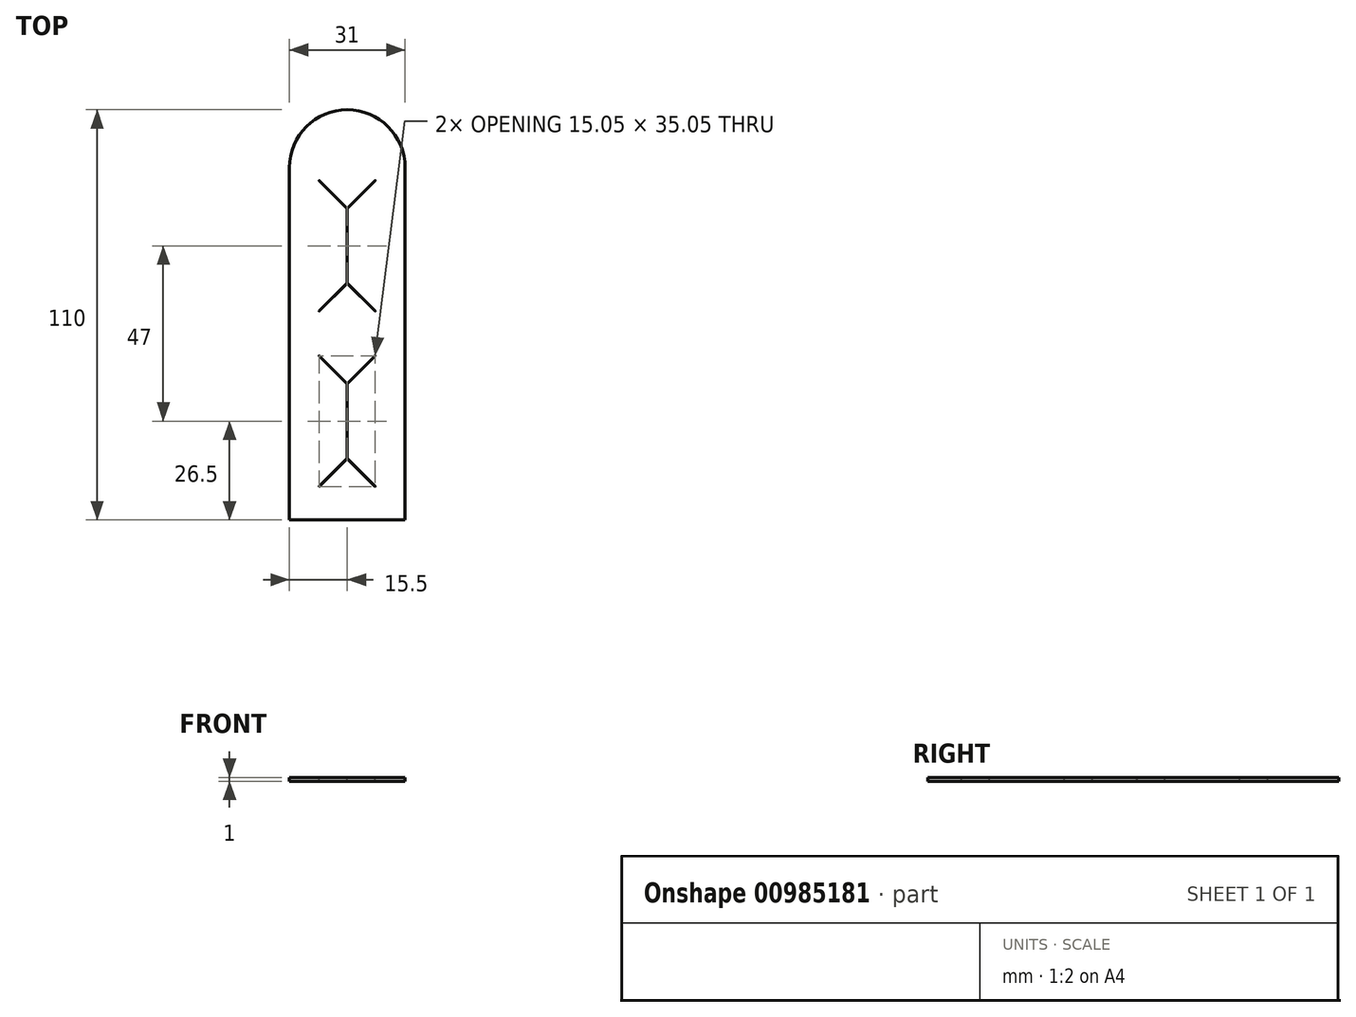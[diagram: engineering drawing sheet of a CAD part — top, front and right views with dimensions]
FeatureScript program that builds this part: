
annotation { "Feature Type Name" : "Feature", "Feature Type Description" : "" }
export const myFeature = defineFeature(function(context is Context, id is Id, definition is map)
    precondition{}
    {
        {
            var Q0;
            Q0=qCreatedBy(makeId("Top.planeOp"),FACE);
            var sketch = newSketch(context, id + "F0", { "sketchPlane" : qUnion([Q0])});
            skLineSegment(sketch, "E0.bottom", {"start": v(0, 0) * mm, "end": v(31, 0) * mm});
            skLineSegment(sketch, "E0.top", {"start": v(0, 94.5) * mm, "end": v(31, 94.5) * mm, "construction": true});
            skLineSegment(sketch, "E0.left", {"start": v(0, 0) * mm, "end": v(0, 94.5) * mm});
            skLineSegment(sketch, "E0.right", {"start": v(31, 0) * mm, "end": v(31, 94.5) * mm});
            skPoint(sketch, "E1", {"position": v(15.5, 94.5) * mm});
            skCircle(sketch, "E2", {"center": v(15.5, 94.5) * mm, "radius": 15.5 * mm, "construction": true});
            skArc(sketch, "E3", {"start": v(31, 94.5) * mm, "mid": v(15.5, 110) * mm, "end": v(0, 94.5) * mm});
            skLineSegment(sketch, "E4", {"start": v(15.5, 110) * mm, "end": v(15.5, 0) * mm, "construction": true});
            skSolve(sketch);
        }
        {
            var Q0;
            Q0 = qSketchRegion(id + "F0", true);
            extrude(context, id + "F1", {"entities" : qUnion([Q0]), "depth" : 1 * mm, "offsetDistance" : 25 * mm});
        }
        {
            var Q0;
            Q0=makeQuery(id+"F1.opExtrude","CAP_FACE",FACE,{"disambiguationData":[OSD([sQuery(id+"F0.wireOp",EDGE,"E0.bottom"),sQuery(id+"F0.wireOp",EDGE,"E0.left"),sQuery(id+"F0.wireOp",EDGE,"E0.right"),sQuery(id+"F0.wireOp",EDGE,"E3")])],"isStart":false});
            var sketch = newSketch(context, id + "F2", { "sketchPlane" : qUnion([Q0])});
            skLineSegment(sketch, "E5.bottom", {"start": v(23, 44) * mm, "end": v(8, 44) * mm, "construction": true});
            skLineSegment(sketch, "E5.top", {"start": v(23, 9) * mm, "end": v(8, 9) * mm, "construction": true});
            skLineSegment(sketch, "E5.left", {"start": v(23, 44) * mm, "end": v(23, 9) * mm, "construction": true});
            skLineSegment(sketch, "E5.right", {"start": v(8, 44) * mm, "end": v(8, 9) * mm, "construction": true});
            skPoint(sketch, "E5.middle", {"position": v(15.5, 26.5) * mm});
            skCircle(sketch, "E6", {"center": v(8, 44) * mm, "radius": 0.03 * mm});
            skCircle(sketch, "E7", {"center": v(23, 44) * mm, "radius": 0.03 * mm});
            skCircle(sketch, "E8", {"center": v(23, 9) * mm, "radius": 0.03 * mm});
            skCircle(sketch, "E9", {"center": v(8, 9) * mm, "radius": 0.03 * mm});
            skLineSegment(sketch, "E10", {"start": v(15.5, 110) * mm, "end": v(15.5, 0) * mm, "construction": true});
            skLineSegment(sketch, "E11", {"start": v(8, 44) * mm, "end": v(15.5, 36.5) * mm, "construction": true});
            skLineSegment(sketch, "E12", {"start": v(15.5, 36.5) * mm, "end": v(23, 44) * mm, "construction": true});
            skPoint(sketch, "E13", {"position": v(15.5, 44) * mm});
            skLineSegment(sketch, "E14", {"start": v(8, 9) * mm, "end": v(15.5, 16.5) * mm, "construction": true});
            skLineSegment(sketch, "E15", {"start": v(15.5, 16.5) * mm, "end": v(23, 9) * mm, "construction": true});
            skCircle(sketch, "E16", {"center": v(15.5, 36.5) * mm, "radius": 0.03 * mm, "construction": true});
            skCircle(sketch, "E17", {"center": v(15.5, 16.5) * mm, "radius": 0.03 * mm, "construction": true});
            skLineSegment(sketch, "E18", {"start": v(15.5, 36.52) * mm, "end": v(22.97, 44) * mm});
            skLineSegment(sketch, "E19", {"start": v(23, 43.98) * mm, "end": v(15.52, 36.5) * mm});
            skLineSegment(sketch, "E20", {"start": v(15.52, 36.5) * mm, "end": v(15.52, 16.5) * mm});
            skLineSegment(sketch, "E21", {"start": v(8, 43.98) * mm, "end": v(15.47, 36.5) * mm});
            skLineSegment(sketch, "E22", {"start": v(15.47, 36.5) * mm, "end": v(15.47, 16.5) * mm});
            skLineSegment(sketch, "E23", {"start": v(15.47, 16.5) * mm, "end": v(8, 9.03) * mm});
            skLineSegment(sketch, "E24", {"start": v(22.97, 9) * mm, "end": v(15.5, 16.48) * mm});
            skLineSegment(sketch, "E25", {"start": v(15.52, 16.5) * mm, "end": v(23, 9.03) * mm});
            skLineSegment(sketch, "E26", {"start": v(8.02, 44) * mm, "end": v(15.5, 36.52) * mm});
            skLineSegment(sketch, "E27", {"start": v(15.5, 16.48) * mm, "end": v(8.02, 9) * mm});
            skLineSegment(sketch, "E28.0.1.0", {"start": v(23, 56) * mm, "end": v(8, 56) * mm, "construction": true});
            skLineSegment(sketch, "E28.0.1.1", {"start": v(15.47, 83.5) * mm, "end": v(15.47, 63.5) * mm});
            skLineSegment(sketch, "E28.0.1.2", {"start": v(15.5, 63.48) * mm, "end": v(8.02, 56) * mm});
            skPoint(sketch, "E28.0.1.3", {"position": v(15.5, 91) * mm});
            skLineSegment(sketch, "E28.0.1.4", {"start": v(15.5, 83.5) * mm, "end": v(23, 91) * mm, "construction": true});
            skLineSegment(sketch, "E28.0.1.5", {"start": v(8, 56) * mm, "end": v(15.5, 63.5) * mm, "construction": true});
            skLineSegment(sketch, "E28.0.1.6", {"start": v(15.52, 83.5) * mm, "end": v(15.52, 63.5) * mm});
            skLineSegment(sketch, "E28.0.1.7", {"start": v(15.5, 63.5) * mm, "end": v(23, 56) * mm, "construction": true});
            skLineSegment(sketch, "E28.0.1.8", {"start": v(15.5, 83.53) * mm, "end": v(22.97, 91) * mm});
            skPoint(sketch, "E28.0.1.9", {"position": v(15.5, 73.5) * mm});
            skLineSegment(sketch, "E28.0.1.10", {"start": v(8, 90.98) * mm, "end": v(15.47, 83.5) * mm});
            skLineSegment(sketch, "E28.0.1.11", {"start": v(23, 91) * mm, "end": v(23, 56) * mm, "construction": true});
            skLineSegment(sketch, "E28.0.1.12", {"start": v(8, 91) * mm, "end": v(8, 56) * mm, "construction": true});
            skLineSegment(sketch, "E28.0.1.13", {"start": v(23, 90.97) * mm, "end": v(15.52, 83.5) * mm});
            skLineSegment(sketch, "E28.0.1.14", {"start": v(15.52, 63.5) * mm, "end": v(23, 56.03) * mm});
            skLineSegment(sketch, "E28.0.1.15", {"start": v(23, 91) * mm, "end": v(8, 91) * mm, "construction": true});
            skLineSegment(sketch, "E28.0.1.16", {"start": v(8, 91) * mm, "end": v(15.5, 83.5) * mm, "construction": true});
            skLineSegment(sketch, "E28.0.1.17", {"start": v(15.47, 63.5) * mm, "end": v(8, 56.03) * mm});
            skLineSegment(sketch, "E28.0.1.18", {"start": v(8.02, 91) * mm, "end": v(15.5, 83.53) * mm});
            skLineSegment(sketch, "E28.0.1.19", {"start": v(22.97, 56) * mm, "end": v(15.5, 63.48) * mm});
            skCircle(sketch, "E28.0.1.20", {"center": v(8, 56) * mm, "radius": 0.03 * mm});
            skCircle(sketch, "E28.0.1.21", {"center": v(15.5, 83.5) * mm, "radius": 0.03 * mm, "construction": true});
            skCircle(sketch, "E28.0.1.22", {"center": v(15.5, 63.5) * mm, "radius": 0.03 * mm, "construction": true});
            skCircle(sketch, "E28.0.1.23", {"center": v(23, 91) * mm, "radius": 0.03 * mm});
            skCircle(sketch, "E28.0.1.24", {"center": v(23, 56) * mm, "radius": 0.03 * mm});
            skCircle(sketch, "E28.0.1.25", {"center": v(8, 91) * mm, "radius": 0.03 * mm});
            skLineSegment(sketch, "E28.direction1", {"start": v(8, 9) * mm, "end": v(33, 9) * mm, "construction": true});
            skLineSegment(sketch, "E28.direction2", {"start": v(8, 9) * mm, "end": v(8, 56) * mm, "construction": true});
            skSolve(sketch);
        }
        {
            var Q0;
            Q0 = qSketchRegion(id + "F2", true);
            extrude(context, id + "F3", {"entities" : qUnion([Q0]), "operationType" : NewBodyOperationType.REMOVE, "oppositeDirection" : true, "depth" : 25 * mm, "offsetDistance" : 25 * mm});
        }
    });
